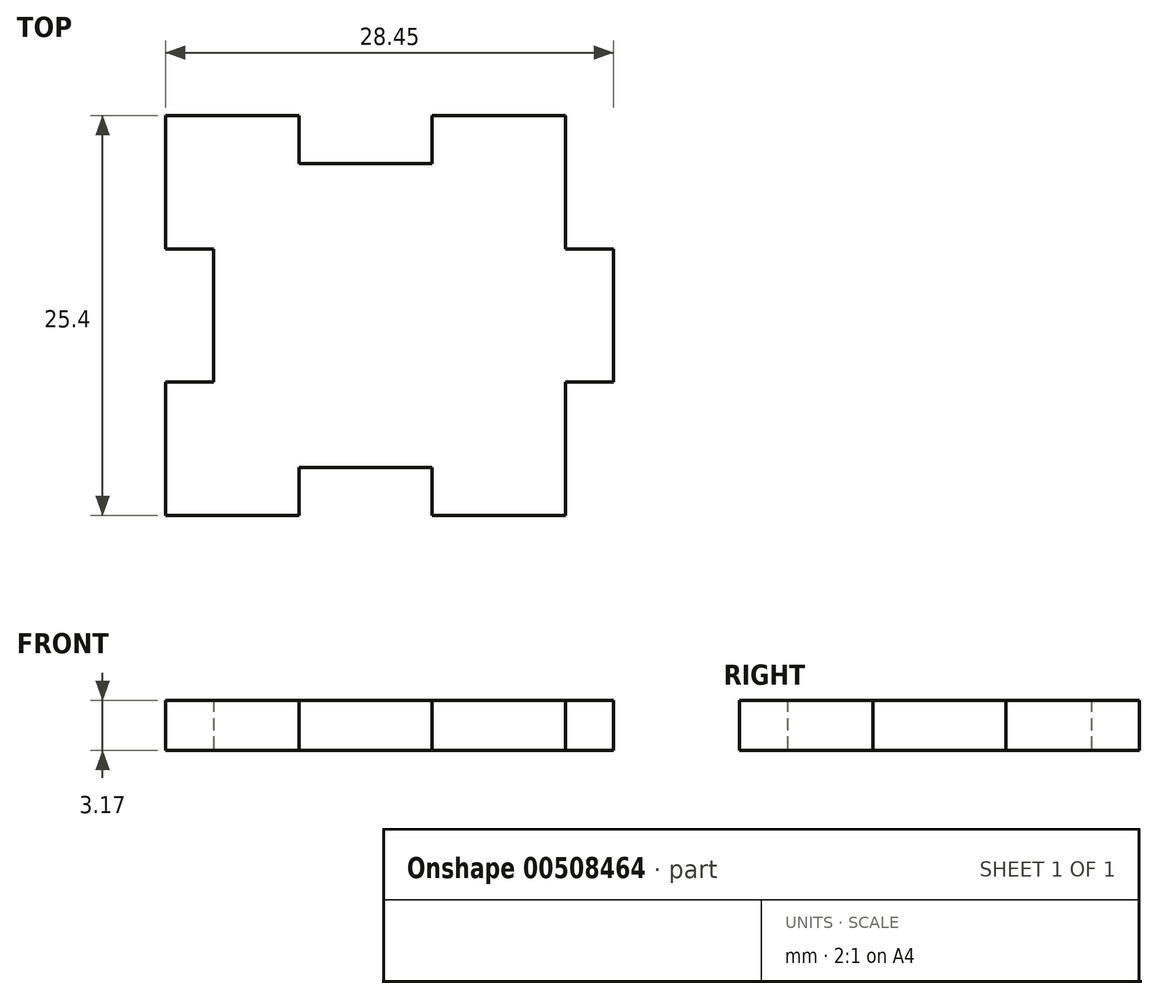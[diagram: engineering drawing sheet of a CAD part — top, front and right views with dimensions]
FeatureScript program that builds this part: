
annotation { "Feature Type Name" : "Feature", "Feature Type Description" : "" }
export const myFeature = defineFeature(function(context is Context, id is Id, definition is map)
    precondition{}
    {
        {
            var Q0;
            Q0=qCreatedBy(makeId("Top.planeOp"),FACE);
            var sketch = newSketch(context, id + "F0", { "sketchPlane" : qUnion([Q0])});
            skLineSegment(sketch, "E0", {"start": v(-27.2, 17.6) * mm, "end": v(-27.2, 9.13) * mm});
            skLineSegment(sketch, "E1", {"start": v(-27.2, 9.13) * mm, "end": v(-24.15, 9.13) * mm});
            skLineSegment(sketch, "E2", {"start": v(-24.15, 9.13) * mm, "end": v(-24.15, 0.66) * mm});
            skLineSegment(sketch, "E3", {"start": v(-24.15, 0.66) * mm, "end": v(-27.2, 0.66) * mm});
            skLineSegment(sketch, "E4", {"start": v(-27.2, 0.66) * mm, "end": v(-27.2, -7.8) * mm});
            skLineSegment(sketch, "E5", {"start": v(-27.2, -7.8) * mm, "end": v(-18.73, -7.8) * mm});
            skLineSegment(sketch, "E6", {"start": v(-18.73, -7.8) * mm, "end": v(-18.73, -4.76) * mm});
            skLineSegment(sketch, "E7", {"start": v(-18.73, -4.76) * mm, "end": v(-10.26, -4.76) * mm});
            skLineSegment(sketch, "E8", {"start": v(-10.26, -4.76) * mm, "end": v(-10.26, -7.8) * mm});
            skLineSegment(sketch, "E9", {"start": v(-10.26, -7.8) * mm, "end": v(-1.8, -7.8) * mm});
            skLineSegment(sketch, "E10", {"start": v(-1.8, -7.8) * mm, "end": v(-1.8, 0.66) * mm});
            skLineSegment(sketch, "E11", {"start": v(-1.8, 0.66) * mm, "end": v(1.25, 0.66) * mm});
            skLineSegment(sketch, "E12", {"start": v(1.25, 0.66) * mm, "end": v(1.25, 9.13) * mm});
            skLineSegment(sketch, "E13", {"start": v(1.25, 9.13) * mm, "end": v(-1.8, 9.13) * mm});
            skLineSegment(sketch, "E14", {"start": v(-1.8, 9.13) * mm, "end": v(-1.8, 17.6) * mm});
            skLineSegment(sketch, "E15", {"start": v(-1.8, 17.6) * mm, "end": v(-10.26, 17.6) * mm});
            skLineSegment(sketch, "E16", {"start": v(-10.26, 17.6) * mm, "end": v(-10.26, 14.55) * mm});
            skLineSegment(sketch, "E17", {"start": v(-10.26, 14.55) * mm, "end": v(-18.73, 14.55) * mm});
            skLineSegment(sketch, "E18", {"start": v(-18.73, 14.55) * mm, "end": v(-18.73, 17.6) * mm});
            skLineSegment(sketch, "E19", {"start": v(-18.73, 17.6) * mm, "end": v(-27.2, 17.6) * mm});
            skSolve(sketch);
        }
        {
            var Q0;
            Q0=makeQuery(id+"F0.imprint","IMPRINT",FACE,{"disambiguationData":[TD([[makeQuery(id+"F0.imprint","IMPRINT",EDGE,{"derivedFrom":sQuery(id+"F0.wireOp",EDGE,"E0")}),1.0]])]});
            extrude(context, id + "F1", {"entities" : qUnion([Q0]), "depth" : 3.17 * mm});
        }
    });
